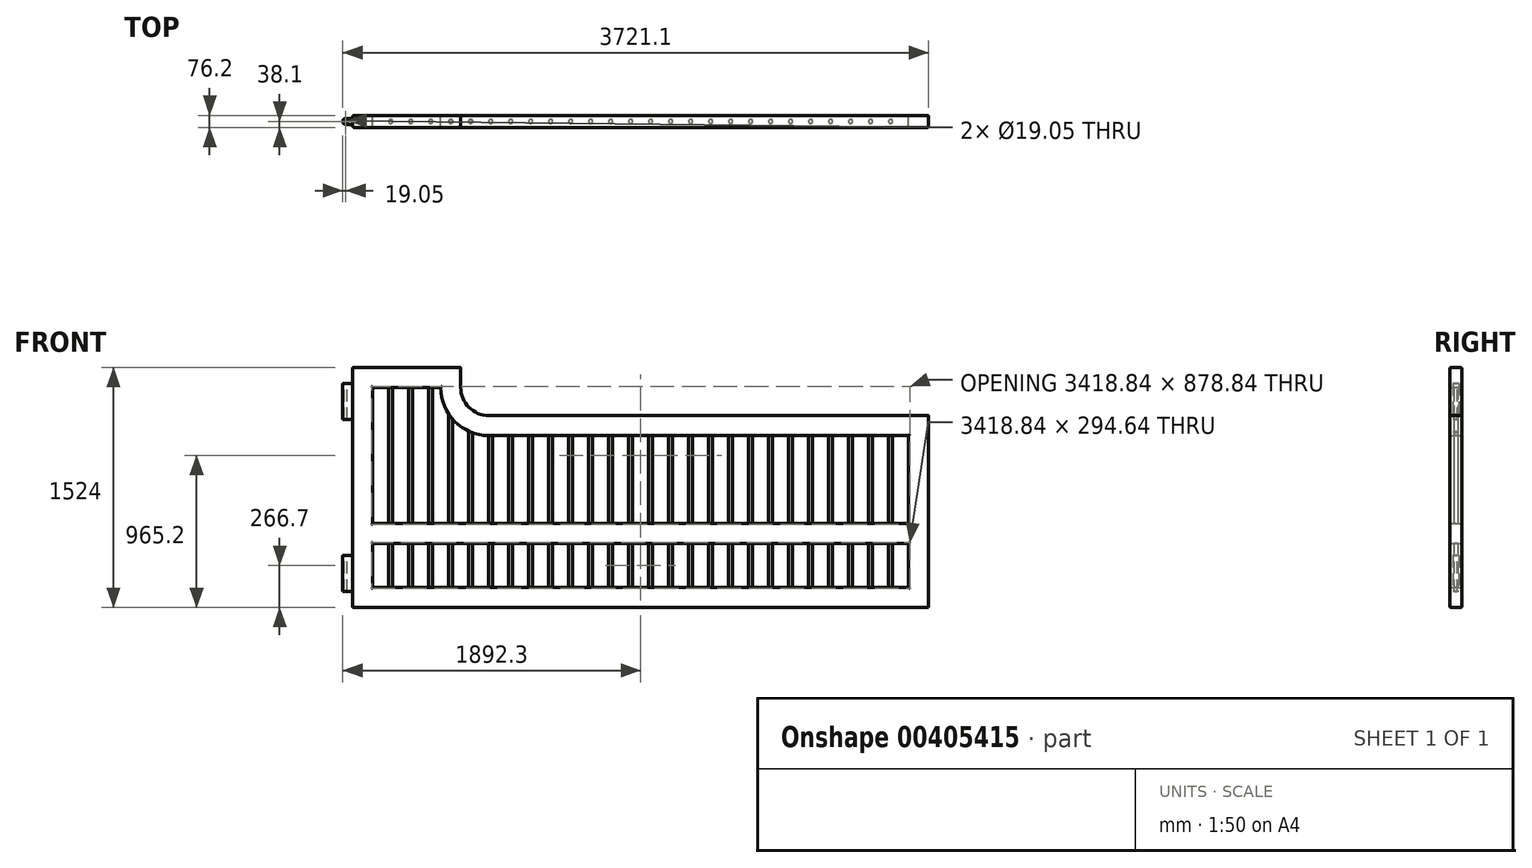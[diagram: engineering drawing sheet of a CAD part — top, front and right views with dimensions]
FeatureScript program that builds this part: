
annotation { "Feature Type Name" : "Feature", "Feature Type Description" : "" }
export const myFeature = defineFeature(function(context is Context, id is Id, definition is map)
    precondition{}
    {
        {
            var Q0;
            Q0=qCreatedBy(makeId("Front.planeOp"),FACE);
            var sketch = newSketch(context, id + "F0", { "sketchPlane" : qUnion([Q0])});
            skLineSegment(sketch, "E0", {"start": v(-1828.8, -609.6) * mm, "end": v(1828.8, -609.6) * mm});
            skLineSegment(sketch, "E1", {"start": v(1828.8, -609.6) * mm, "end": v(1828.8, 609.6) * mm});
            skLineSegment(sketch, "E2", {"start": v(1828.8, 609.6) * mm, "end": v(-965.2, 609.6) * mm});
            skLineSegment(sketch, "E3", {"start": v(-1828.8, -609.6) * mm, "end": v(-1828.8, 914.4) * mm});
            skLineSegment(sketch, "E4", {"start": v(-1828.8, 914.4) * mm, "end": v(-1143, 914.4) * mm});
            skLineSegment(sketch, "E5.bottom", {"start": v(-1701.8, -203.2) * mm, "end": v(1701.8, -203.2) * mm});
            skLineSegment(sketch, "E5.top", {"start": v(-1701.8, -482.6) * mm, "end": v(1701.8, -482.6) * mm});
            skLineSegment(sketch, "E5.left", {"start": v(-1701.8, -203.2) * mm, "end": v(-1701.8, -482.6) * mm});
            skLineSegment(sketch, "E5.right", {"start": v(1701.8, -203.2) * mm, "end": v(1701.8, -482.6) * mm});
            skLineSegment(sketch, "E6", {"start": v(-1270, 787.4) * mm, "end": v(-1701.8, 787.4) * mm});
            skLineSegment(sketch, "E7", {"start": v(-1701.8, 787.4) * mm, "end": v(-1701.8, -76.2) * mm});
            skLineSegment(sketch, "E8", {"start": v(1701.8, -76.2) * mm, "end": v(1701.8, 482.6) * mm});
            skLineSegment(sketch, "E9", {"start": v(1701.8, 482.6) * mm, "end": v(-965.2, 482.6) * mm});
            skLineSegment(sketch, "E10", {"start": v(-1701.8, -76.2) * mm, "end": v(1701.8, -76.2) * mm});
            skLineSegment(sketch, "E11", {"start": v(-1143, 914.4) * mm, "end": v(-1143, 787.4) * mm});
            skArc(sketch, "E12", {"start": v(-965.2, 609.6) * mm, "mid": v(-1090.92, 661.68) * mm, "end": v(-1143, 787.4) * mm});
            skArc(sketch, "E13", {"start": v(-965.2, 482.6) * mm, "mid": v(-1180.73, 571.87) * mm, "end": v(-1270, 787.4) * mm});
            skSolve(sketch);
        }
        {
            var Q0;
            Q0=makeQuery(id+"F0.imprint","IMPRINT",FACE,{"disambiguationData":[TD([[makeQuery(id+"F0.imprint","IMPRINT",EDGE,{"derivedFrom":sQuery(id+"F0.wireOp",EDGE,"E0")}),1.0]])]});
            extrude(context, id + "F1", {"entities" : qUnion([Q0]), "depth" : 76.2 * mm, "symmetric" : true});
        }
        {
            var Q0;
            Q0=makeQuery(id+"F1.opExtrude","CAP_FACE",FACE,{"disambiguationData":[OSD([sQuery(id+"F0.wireOp",EDGE,"E0"),sQuery(id+"F0.wireOp",EDGE,"E1"),sQuery(id+"F0.wireOp",EDGE,"E2"),sQuery(id+"F0.wireOp",EDGE,"E3"),sQuery(id+"F0.wireOp",EDGE,"E4"),sQuery(id+"F0.wireOp",EDGE,"45394d91-6a49-4310-a277-840086c14d09"),sQuery(id+"F0.wireOp",EDGE,"E5.bottom"),sQuery(id+"F0.wireOp",EDGE,"E5.top"),sQuery(id+"F0.wireOp",EDGE,"E5.left"),sQuery(id+"F0.wireOp",EDGE,"E5.right"),sQuery(id+"F0.wireOp",EDGE,"E6"),sQuery(id+"F0.wireOp",EDGE,"E7"),sQuery(id+"F0.wireOp",EDGE,"E8"),sQuery(id+"F0.wireOp",EDGE,"E9"),sQuery(id+"F0.wireOp",EDGE,"70122fbd-1a25-48f8-8ea5-0eddc12a5df7"),sQuery(id+"F0.wireOp",EDGE,"E10")])],"isStart":true});
            var Q1;
            Q1=makeQuery(id+"F1.opExtrude","CAP_FACE",FACE,{"disambiguationData":[OSD([sQuery(id+"F0.wireOp",EDGE,"E0"),sQuery(id+"F0.wireOp",EDGE,"E1"),sQuery(id+"F0.wireOp",EDGE,"E2"),sQuery(id+"F0.wireOp",EDGE,"E3"),sQuery(id+"F0.wireOp",EDGE,"E4"),sQuery(id+"F0.wireOp",EDGE,"45394d91-6a49-4310-a277-840086c14d09"),sQuery(id+"F0.wireOp",EDGE,"E5.bottom"),sQuery(id+"F0.wireOp",EDGE,"E5.top"),sQuery(id+"F0.wireOp",EDGE,"E5.left"),sQuery(id+"F0.wireOp",EDGE,"E5.right"),sQuery(id+"F0.wireOp",EDGE,"E6"),sQuery(id+"F0.wireOp",EDGE,"E7"),sQuery(id+"F0.wireOp",EDGE,"E8"),sQuery(id+"F0.wireOp",EDGE,"E9"),sQuery(id+"F0.wireOp",EDGE,"70122fbd-1a25-48f8-8ea5-0eddc12a5df7"),sQuery(id+"F0.wireOp",EDGE,"E10")])],"isStart":false});
            fillet(context, id + "F2", {"entities" : qUnion([Q0, Q1]), "radius" : 7.62 * mm, "tangentPropagation" : true, "allowEdgeOverflow" : false});
        }
        {
            var Q0;
            Q0=makeQuery(id+"F1.opExtrude","SWEPT_FACE",FACE,{"disambiguationData":[OSD([sQuery(id+"F0.wireOp",EDGE,"E5.top")])]});
            var sketch = newSketch(context, id + "F3", { "sketchPlane" : qUnion([Q0])});
            skLineSegment(sketch, "E14", {"start": v(-1701.8, 0) * mm, "end": v(1701.8, 0) * mm, "construction": true});
            skCircle(sketch, "E15", {"center": v(-1587.5, 0) * mm, "radius": 12.7 * mm});
            skCircle(sketch, "E16.1.0.0", {"center": v(-1460.5, 0) * mm, "radius": 12.7 * mm});
            skCircle(sketch, "E16.2.0.0", {"center": v(-1333.5, 0) * mm, "radius": 12.7 * mm});
            skCircle(sketch, "E16.3.0.0", {"center": v(-1206.5, 0) * mm, "radius": 12.7 * mm});
            skCircle(sketch, "E16.4.0.0", {"center": v(-1079.5, 0) * mm, "radius": 12.7 * mm});
            skCircle(sketch, "E16.5.0.0", {"center": v(-952.5, 0) * mm, "radius": 12.7 * mm});
            skCircle(sketch, "E16.6.0.0", {"center": v(-825.5, 0) * mm, "radius": 12.7 * mm});
            skCircle(sketch, "E16.7.0.0", {"center": v(-698.5, 0) * mm, "radius": 12.7 * mm});
            skCircle(sketch, "E16.8.0.0", {"center": v(-571.5, 0) * mm, "radius": 12.7 * mm});
            skCircle(sketch, "E16.9.0.0", {"center": v(-444.5, 0) * mm, "radius": 12.7 * mm});
            skCircle(sketch, "E16.10.0.0", {"center": v(-317.5, 0) * mm, "radius": 12.7 * mm});
            skCircle(sketch, "E16.11.0.0", {"center": v(-190.5, 0) * mm, "radius": 12.7 * mm});
            skCircle(sketch, "E16.12.0.0", {"center": v(-63.5, 0) * mm, "radius": 12.7 * mm});
            skCircle(sketch, "E16.13.0.0", {"center": v(63.5, 0) * mm, "radius": 12.7 * mm});
            skCircle(sketch, "E16.14.0.0", {"center": v(190.5, 0) * mm, "radius": 12.7 * mm});
            skCircle(sketch, "E16.15.0.0", {"center": v(317.5, 0) * mm, "radius": 12.7 * mm});
            skCircle(sketch, "E16.16.0.0", {"center": v(444.5, 0) * mm, "radius": 12.7 * mm});
            skCircle(sketch, "E16.17.0.0", {"center": v(571.5, 0) * mm, "radius": 12.7 * mm});
            skCircle(sketch, "E16.18.0.0", {"center": v(698.5, 0) * mm, "radius": 12.7 * mm});
            skCircle(sketch, "E16.19.0.0", {"center": v(825.5, 0) * mm, "radius": 12.7 * mm});
            skCircle(sketch, "E16.20.0.0", {"center": v(952.5, 0) * mm, "radius": 12.7 * mm});
            skCircle(sketch, "E16.21.0.0", {"center": v(1079.5, 0) * mm, "radius": 12.7 * mm});
            skCircle(sketch, "E16.22.0.0", {"center": v(1206.5, 0) * mm, "radius": 12.7 * mm});
            skCircle(sketch, "E16.23.0.0", {"center": v(1333.5, 0) * mm, "radius": 12.7 * mm});
            skCircle(sketch, "E16.24.0.0", {"center": v(1460.5, 0) * mm, "radius": 12.7 * mm});
            skLineSegment(sketch, "E16.direction1", {"start": v(-1587.5, 0) * mm, "end": v(-1460.5, 0) * mm, "construction": true});
            skCircle(sketch, "E17.0.25.0", {"center": v(1587.5, 0) * mm, "radius": 12.7 * mm});
            skSolve(sketch);
        }
        {
            var Q0;
            Q0=makeQuery(id+"F1.opExtrude","SWEPT_FACE",FACE,{"disambiguationData":[OSD([sQuery(id+"F0.wireOp",EDGE,"E3")])]});
            var sketch = newSketch(context, id + "F4", { "sketchPlane" : qUnion([Q0])});
            skLineSegment(sketch, "E18.bottom", {"start": v(-19.05, 812.8) * mm, "end": v(19.05, 812.8) * mm});
            skLineSegment(sketch, "E18.top", {"start": v(-19.05, 584.2) * mm, "end": v(19.05, 584.2) * mm});
            skLineSegment(sketch, "E18.left", {"start": v(-19.05, 812.8) * mm, "end": v(-19.05, 584.2) * mm});
            skLineSegment(sketch, "E18.right", {"start": v(19.05, 812.8) * mm, "end": v(19.05, 584.2) * mm});
            skLineSegment(sketch, "E19.bottom", {"start": v(-19.05, -279.4) * mm, "end": v(19.05, -279.4) * mm});
            skLineSegment(sketch, "E19.top", {"start": v(-19.05, -508) * mm, "end": v(19.05, -508) * mm});
            skLineSegment(sketch, "E19.left", {"start": v(-19.05, -279.4) * mm, "end": v(-19.05, -508) * mm});
            skLineSegment(sketch, "E19.right", {"start": v(19.05, -279.4) * mm, "end": v(19.05, -508) * mm});
            skSolve(sketch);
        }
        {
            var Q0;
            Q0=makeQuery(id+"F4.imprint","IMPRINT",FACE,{"disambiguationData":[TD([[makeQuery(id+"F4.imprint","IMPRINT",EDGE,{"derivedFrom":sQuery(id+"F4.wireOp",EDGE,"E18.bottom")}),-1.0]])]});
            var Q1;
            Q1=makeQuery(id+"F4.imprint","IMPRINT",FACE,{"disambiguationData":[TD([[makeQuery(id+"F4.imprint","IMPRINT",EDGE,{"derivedFrom":sQuery(id+"F4.wireOp",EDGE,"E19.bottom")}),-1.0]])]});
            extrude(context, id + "F5", {"entities" : qUnion([Q0, Q1]), "operationType" : NewBodyOperationType.ADD, "depth" : 63.5 * mm});
        }
        {
            var Q0;
            Q0=makeQuery(id+"F5.opExtrude","CAP_EDGE",EDGE,{"disambiguationData":[OSD([sQuery(id+"F4.wireOp",EDGE,"E18.right")])],"isStart":false});
            var Q1;
            Q1=makeQuery(id+"F5.opExtrude","CAP_EDGE",EDGE,{"disambiguationData":[OSD([sQuery(id+"F4.wireOp",EDGE,"E18.left")])],"isStart":false});
            var Q2;
            Q2=makeQuery(id+"F5.opExtrude","CAP_EDGE",EDGE,{"disambiguationData":[OSD([sQuery(id+"F4.wireOp",EDGE,"E19.right")])],"isStart":false});
            var Q3;
            Q3=makeQuery(id+"F5.opExtrude","CAP_EDGE",EDGE,{"disambiguationData":[OSD([sQuery(id+"F4.wireOp",EDGE,"E19.left")])],"isStart":false});
            fillet(context, id + "F6", {"entities" : qUnion([Q0, Q1, Q2, Q3]), "radius" : 19.05 * mm, "tangentPropagation" : true, "allowEdgeOverflow" : false});
        }
        {
            var Q0;
            Q0=makeQuery(id+"F5.opExtrude","SWEPT_FACE",FACE,{"disambiguationData":[OSD([sQuery(id+"F4.wireOp",EDGE,"E18.bottom")])]});
            var sketch = newSketch(context, id + "F7", { "sketchPlane" : qUnion([Q0])});
            skCircle(sketch, "E20", {"center": v(-1873.25, 0) * mm, "radius": 9.53 * mm});
            skSolve(sketch);
        }
        {
            var Q0;
            Q0=makeQuery(id+"F7.imprint","IMPRINT",FACE,{"disambiguationData":[TD([[makeQuery(id+"F7.imprint","IMPRINT",EDGE,{"derivedFrom":sQuery(id+"F7.wireOp",EDGE,"E20")}),1.0]])]});
            extrude(context, id + "F8", {"entities" : qUnion([Q0]), "operationType" : NewBodyOperationType.REMOVE, "endBound" : BoundingType.THROUGH_ALL, "oppositeDirection" : true, "depth" : 25.4 * mm});
        }
        {
            var Q0;
            Q0=makeQuery(id+"F3.imprint","IMPRINT",FACE,{"disambiguationData":[TD([[makeQuery(id+"F3.imprint","IMPRINT",EDGE,{"derivedFrom":sQuery(id+"F3.wireOp",EDGE,"E16.8.0.0")}),1.0]])]});
            var Q1;
            Q1=makeQuery(id+"F3.imprint","IMPRINT",FACE,{"disambiguationData":[TD([[makeQuery(id+"F3.imprint","IMPRINT",EDGE,{"derivedFrom":sQuery(id+"F3.wireOp",EDGE,"E16.11.0.0")}),1.0]])]});
            var Q2;
            Q2=makeQuery(id+"F3.imprint","IMPRINT",FACE,{"disambiguationData":[TD([[makeQuery(id+"F3.imprint","IMPRINT",EDGE,{"derivedFrom":sQuery(id+"F3.wireOp",EDGE,"E16.14.0.0")}),1.0]])]});
            var Q3;
            Q3=makeQuery(id+"F3.imprint","IMPRINT",FACE,{"disambiguationData":[TD([[makeQuery(id+"F3.imprint","IMPRINT",EDGE,{"derivedFrom":sQuery(id+"F3.wireOp",EDGE,"E16.6.0.0")}),1.0]])]});
            var Q4;
            Q4=makeQuery(id+"F3.imprint","IMPRINT",FACE,{"disambiguationData":[TD([[makeQuery(id+"F3.imprint","IMPRINT",EDGE,{"derivedFrom":sQuery(id+"F3.wireOp",EDGE,"E16.13.0.0")}),1.0]])]});
            var Q5;
            Q5=makeQuery(id+"F3.imprint","IMPRINT",FACE,{"disambiguationData":[TD([[makeQuery(id+"F3.imprint","IMPRINT",EDGE,{"derivedFrom":sQuery(id+"F3.wireOp",EDGE,"E16.7.0.0")}),1.0]])]});
            var Q6;
            Q6=makeQuery(id+"F3.imprint","IMPRINT",FACE,{"disambiguationData":[TD([[makeQuery(id+"F3.imprint","IMPRINT",EDGE,{"derivedFrom":sQuery(id+"F3.wireOp",EDGE,"E16.9.0.0")}),1.0]])]});
            var Q7;
            Q7=makeQuery(id+"F3.imprint","IMPRINT",FACE,{"disambiguationData":[TD([[makeQuery(id+"F3.imprint","IMPRINT",EDGE,{"derivedFrom":sQuery(id+"F3.wireOp",EDGE,"E16.5.0.0")}),1.0]])]});
            var Q8;
            Q8=makeQuery(id+"F3.imprint","IMPRINT",FACE,{"disambiguationData":[TD([[makeQuery(id+"F3.imprint","IMPRINT",EDGE,{"derivedFrom":sQuery(id+"F3.wireOp",EDGE,"E16.4.0.0")}),1.0]])]});
            var Q9;
            Q9=makeQuery(id+"F3.imprint","IMPRINT",FACE,{"disambiguationData":[TD([[makeQuery(id+"F3.imprint","IMPRINT",EDGE,{"derivedFrom":sQuery(id+"F3.wireOp",EDGE,"E16.15.0.0")}),1.0]])]});
            var Q10;
            Q10=makeQuery(id+"F3.imprint","IMPRINT",FACE,{"disambiguationData":[TD([[makeQuery(id+"F3.imprint","IMPRINT",EDGE,{"derivedFrom":sQuery(id+"F3.wireOp",EDGE,"E16.10.0.0")}),1.0]])]});
            var Q11;
            Q11=makeQuery(id+"F3.imprint","IMPRINT",FACE,{"disambiguationData":[TD([[makeQuery(id+"F3.imprint","IMPRINT",EDGE,{"derivedFrom":sQuery(id+"F3.wireOp",EDGE,"E16.12.0.0")}),1.0]])]});
            var Q12;
            Q12=makeQuery(id+"F3.imprint","IMPRINT",FACE,{"disambiguationData":[TD([[makeQuery(id+"F3.imprint","IMPRINT",EDGE,{"derivedFrom":sQuery(id+"F3.wireOp",EDGE,"E16.17.0.0")}),1.0]])]});
            var Q13;
            Q13=makeQuery(id+"F3.imprint","IMPRINT",FACE,{"disambiguationData":[TD([[makeQuery(id+"F3.imprint","IMPRINT",EDGE,{"derivedFrom":sQuery(id+"F3.wireOp",EDGE,"E16.19.0.0")}),1.0]])]});
            var Q14;
            Q14=makeQuery(id+"F3.imprint","IMPRINT",FACE,{"disambiguationData":[TD([[makeQuery(id+"F3.imprint","IMPRINT",EDGE,{"derivedFrom":sQuery(id+"F3.wireOp",EDGE,"E16.18.0.0")}),1.0]])]});
            var Q15;
            Q15=makeQuery(id+"F3.imprint","IMPRINT",FACE,{"disambiguationData":[TD([[makeQuery(id+"F3.imprint","IMPRINT",EDGE,{"derivedFrom":sQuery(id+"F3.wireOp",EDGE,"E16.16.0.0")}),1.0]])]});
            var Q16;
            Q16=makeQuery(id+"F3.imprint","IMPRINT",FACE,{"disambiguationData":[TD([[makeQuery(id+"F3.imprint","IMPRINT",EDGE,{"derivedFrom":sQuery(id+"F3.wireOp",EDGE,"E16.20.0.0")}),1.0]])]});
            var Q17;
            Q17=makeQuery(id+"F3.imprint","IMPRINT",FACE,{"disambiguationData":[TD([[makeQuery(id+"F3.imprint","IMPRINT",EDGE,{"derivedFrom":sQuery(id+"F3.wireOp",EDGE,"E16.23.0.0")}),1.0]])]});
            var Q18;
            Q18=makeQuery(id+"F3.imprint","IMPRINT",FACE,{"disambiguationData":[TD([[makeQuery(id+"F3.imprint","IMPRINT",EDGE,{"derivedFrom":sQuery(id+"F3.wireOp",EDGE,"E16.24.0.0")}),1.0]])]});
            var Q19;
            Q19=makeQuery(id+"F3.imprint","IMPRINT",FACE,{"disambiguationData":[TD([[makeQuery(id+"F3.imprint","IMPRINT",EDGE,{"derivedFrom":sQuery(id+"F3.wireOp",EDGE,"E16.22.0.0")}),1.0]])]});
            var Q20;
            Q20=makeQuery(id+"F3.imprint","IMPRINT",FACE,{"disambiguationData":[TD([[makeQuery(id+"F3.imprint","IMPRINT",EDGE,{"derivedFrom":sQuery(id+"F3.wireOp",EDGE,"E16.21.0.0")}),1.0]])]});
            var Q21;
            Q21=makeQuery(id+"F3.imprint","IMPRINT",FACE,{"disambiguationData":[TD([[makeQuery(id+"F3.imprint","IMPRINT",EDGE,{"derivedFrom":sQuery(id+"F3.wireOp",EDGE,"E17.0.25.0")}),1.0]])]});
            extrude(context, id + "F9", {"entities" : qUnion([Q0, Q1, Q2, Q3, Q4, Q5, Q6, Q7, Q8, Q9, Q10, Q11, Q12, Q13, Q14, Q15, Q16, Q17, Q18, Q19, Q20, Q21]), "operationType" : NewBodyOperationType.ADD, "depth" : 1066.8 * mm});
        }
        {
            var Q0;
            Q0=makeQuery(id+"F3.imprint","IMPRINT",FACE,{"disambiguationData":[TD([[makeQuery(id+"F3.imprint","IMPRINT",EDGE,{"derivedFrom":sQuery(id+"F3.wireOp",EDGE,"E16.2.0.0")}),1.0]])]});
            var Q1;
            Q1=makeQuery(id+"F3.imprint","IMPRINT",FACE,{"disambiguationData":[TD([[makeQuery(id+"F3.imprint","IMPRINT",EDGE,{"derivedFrom":sQuery(id+"F3.wireOp",EDGE,"E16.3.0.0")}),1.0]])]});
            var Q2;
            Q2=makeQuery(id+"F3.imprint","IMPRINT",FACE,{"disambiguationData":[TD([[makeQuery(id+"F3.imprint","IMPRINT",EDGE,{"derivedFrom":sQuery(id+"F3.wireOp",EDGE,"E16.1.0.0")}),1.0]])]});
            var Q3;
            Q3=makeQuery(id+"F3.imprint","IMPRINT",FACE,{"disambiguationData":[TD([[makeQuery(id+"F3.imprint","IMPRINT",EDGE,{"derivedFrom":sQuery(id+"F3.wireOp",EDGE,"E15")}),1.0]])]});
            extrude(context, id + "F10", {"entities" : qUnion([Q0, Q1, Q2, Q3]), "operationType" : NewBodyOperationType.ADD, "depth" : 1384.3 * mm});
        }
    });
